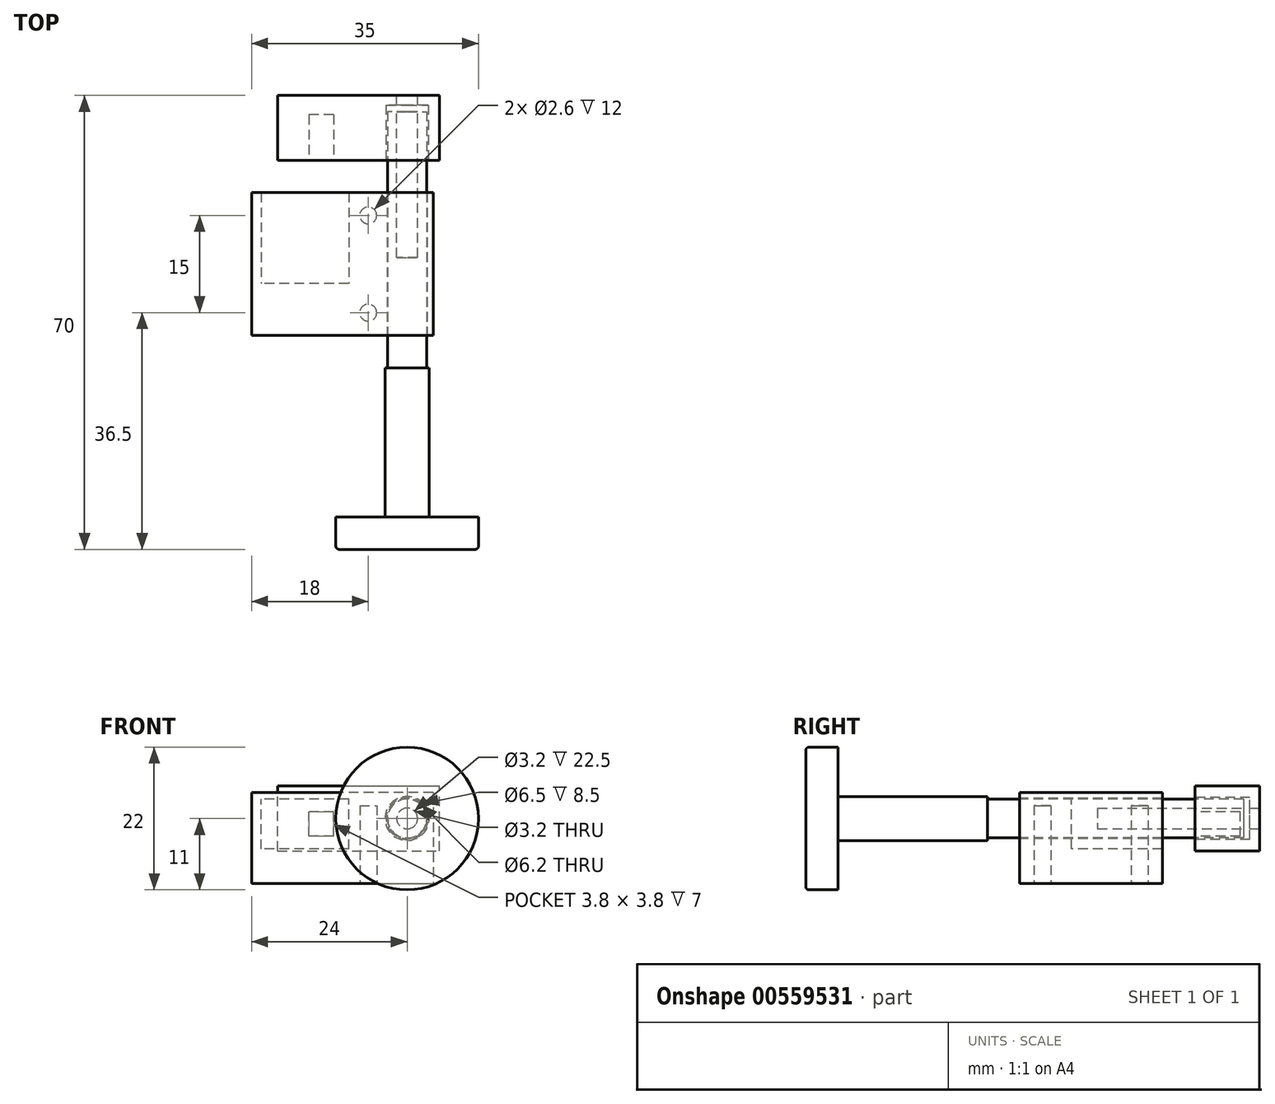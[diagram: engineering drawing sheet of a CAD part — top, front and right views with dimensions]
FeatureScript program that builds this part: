
annotation { "Feature Type Name" : "Feature", "Feature Type Description" : "" }
export const myFeature = defineFeature(function(context is Context, id is Id, definition is map)
    precondition{}
    {
        {
            var Q0;
            Q0=qCreatedBy(makeId("Front.planeOp"),FACE);
            var sketch = newSketch(context, id + "F0", { "sketchPlane" : qUnion([Q0])});
            skLineSegment(sketch, "E0.bottom", {"start": v(-22, -4.85) * mm, "end": v(-50, -4.85) * mm});
            skLineSegment(sketch, "E0.top", {"start": v(-22, 4.85) * mm, "end": v(-50, 4.85) * mm});
            skLineSegment(sketch, "E0.left", {"start": v(-22, -4.85) * mm, "end": v(-22, 4.85) * mm});
            skLineSegment(sketch, "E0.right", {"start": v(-50, -4.85) * mm, "end": v(-50, 4.85) * mm});
            skPoint(sketch, "E0.middle", {"position": v(-36, 0) * mm});
            skLineSegment(sketch, "E1.bottom", {"start": v(-35, -3.85) * mm, "end": v(-48.5, -3.85) * mm});
            skLineSegment(sketch, "E1.top", {"start": v(-35, 3.85) * mm, "end": v(-48.5, 3.85) * mm});
            skLineSegment(sketch, "E1.left", {"start": v(-35, -3.85) * mm, "end": v(-35, 3.85) * mm});
            skLineSegment(sketch, "E1.right", {"start": v(-48.5, -3.85) * mm, "end": v(-48.5, 3.85) * mm});
            skPoint(sketch, "E1.middle", {"position": v(-41.75, 0) * mm});
            skLineSegment(sketch, "E2.bottom", {"start": v(-50, -4.85) * mm, "end": v(-22, -4.85) * mm});
            skLineSegment(sketch, "E2.top", {"start": v(-50, -9.15) * mm, "end": v(-22, -9.15) * mm});
            skLineSegment(sketch, "E2.left", {"start": v(-50, -4.85) * mm, "end": v(-50, -9.15) * mm});
            skLineSegment(sketch, "E2.right", {"start": v(-22, -4.85) * mm, "end": v(-22, -9.15) * mm});
            skCircle(sketch, "E3", {"center": v(-26, 0.85) * mm, "radius": 3.1 * mm});
            skSolve(sketch);
        }
        {
            var Q0;
            Q0=qSketchRegion(id+"F0",true);
            extrude(context, id + "F1", {"entities" : qUnion([Q0]), "oppositeDirection" : true, "depth" : 22 * mm});
        }
        {
            var Q0;
            Q0=makeQuery(id+"F1.opExtrude","CAP_FACE",FACE,{"disambiguationData":[OSD([sQuery(id+"F0.wireOp",EDGE,"E0.bottom"),sQuery(id+"F0.wireOp",EDGE,"E0.top"),sQuery(id+"F0.wireOp",EDGE,"E0.left"),sQuery(id+"F0.wireOp",EDGE,"E0.right"),sQuery(id+"F0.wireOp",EDGE,"E1.bottom"),sQuery(id+"F0.wireOp",EDGE,"E1.top"),sQuery(id+"F0.wireOp",EDGE,"E1.left"),sQuery(id+"F0.wireOp",EDGE,"E1.right"),sQuery(id+"F0.wireOp",EDGE,"IlVQ0T6Q-kpas-WKJO-rE1o-QIE4vgIgB8Sl")])],"isStart":true});
            var sketch = newSketch(context, id + "F2", { "sketchPlane" : qUnion([Q0])});
            skLineSegment(sketch, "E4.bottom", {"start": v(-48.5, 3.85) * mm, "end": v(-35, 3.85) * mm});
            skLineSegment(sketch, "E4.top", {"start": v(-48.5, -3.85) * mm, "end": v(-35, -3.85) * mm});
            skLineSegment(sketch, "E4.left", {"start": v(-35, 3.85) * mm, "end": v(-35, -3.85) * mm});
            skLineSegment(sketch, "E4.right", {"start": v(-48.5, 3.85) * mm, "end": v(-48.5, -3.85) * mm});
            skSolve(sketch);
        }
        {
            var Q0;
            Q0=qSketchRegion(id+"F2",true);
            extrude(context, id + "F3", {"entities" : qUnion([Q0]), "operationType" : NewBodyOperationType.ADD, "oppositeDirection" : true, "depth" : 8 * mm});
        }
        {
            var Q0;
            Q0=makeQuery(id+"F1.opExtrude","SWEPT_FACE",FACE,{"disambiguationData":[OSD([sQuery(id+"F0.wireOp",EDGE,"E2.top")])]});
            var sketch = newSketch(context, id + "F4", { "sketchPlane" : qUnion([Q0])});
            skCircle(sketch, "E5", {"center": v(-32, -3.5) * mm, "radius": 1.3 * mm});
            skCircle(sketch, "E6", {"center": v(-32, -18.5) * mm, "radius": 1.3 * mm});
            skSolve(sketch);
        }
        {
            var Q0;
            Q0=qSketchRegion(id+"F4",true);
            extrude(context, id + "F5", {"entities" : qUnion([Q0]), "operationType" : NewBodyOperationType.REMOVE, "oppositeDirection" : true, "depth" : 12 * mm});
        }
        {
            var Q0;
            Q0=makeQuery(id+"F1.opExtrude","CAP_FACE",FACE,{"disambiguationData":[OSD([sQuery(id+"F0.wireOp",EDGE,"E0.top"),sQuery(id+"F0.wireOp",EDGE,"E0.left"),sQuery(id+"F0.wireOp",EDGE,"E0.right"),sQuery(id+"F0.wireOp",EDGE,"E1.bottom"),sQuery(id+"F0.wireOp",EDGE,"E1.top"),sQuery(id+"F0.wireOp",EDGE,"E1.left"),sQuery(id+"F0.wireOp",EDGE,"E1.right"),sQuery(id+"F0.wireOp",EDGE,"E2.top"),sQuery(id+"F0.wireOp",EDGE,"E2.left"),sQuery(id+"F0.wireOp",EDGE,"E2.right"),sQuery(id+"F0.wireOp",EDGE,"E3")])],"isStart":false});
            cPlane(context, id + "F6", {"entities" : qUnion([Q0]), "cplaneType" : CPlaneType.OFFSET, "offset" : 5 * mm, "width" : 150 * mm, "height" : 150 * mm});
        }
        {
            var Q0;
            Q0=qCreatedBy(makeId("Front.planeOp"),FACE);
            cPlane(context, id + "F7", {"entities" : qUnion([Q0]), "cplaneType" : CPlaneType.OFFSET, "offset" : 28 * mm, "width" : 150 * mm, "height" : 150 * mm});
        }
        {
            var Q0;
            Q0=qCreatedBy(id+"F7.planeOp",FACE);
            var sketch = newSketch(context, id + "F8", { "sketchPlane" : qUnion([Q0])});
            skCircle(sketch, "E7", {"center": v(-26, 0.85) * mm, "radius": 11 * mm});
            skSolve(sketch);
        }
        {
            var Q0;
            Q0=qSketchRegion(id+"F8",true);
            extrude(context, id + "F9", {"entities" : qUnion([Q0]), "depth" : 5 * mm});
        }
        {
            var Q0;
            Q0=makeQuery(id+"F9.opExtrude","CAP_FACE",FACE,{"disambiguationData":[OSD([sQuery(id+"F8.wireOp",EDGE,"E7")])],"isStart":true});
            var sketch = newSketch(context, id + "F10", { "sketchPlane" : qUnion([Q0])});
            skCircle(sketch, "E8", {"center": v(26, 0.85) * mm, "radius": 3 * mm});
            skSolve(sketch);
        }
        {
            var Q0;
            Q0=qSketchRegion(id+"F10",true);
            extrude(context, id + "F11", {"entities" : qUnion([Q0]), "operationType" : NewBodyOperationType.ADD, "depth" : 55 * mm});
        }
        {
            var Q0;
            Q0=qCreatedBy(id+"F6.planeOp",FACE);
            var sketch = newSketch(context, id + "F12", { "sketchPlane" : qUnion([Q0])});
            skLineSegment(sketch, "E9.bottom", {"start": v(46, -4.15) * mm, "end": v(21, -4.15) * mm});
            skLineSegment(sketch, "E9.top", {"start": v(46, 5.85) * mm, "end": v(21, 5.85) * mm});
            skLineSegment(sketch, "E9.left", {"start": v(46, -4.15) * mm, "end": v(46, 5.85) * mm});
            skLineSegment(sketch, "E9.right", {"start": v(21, -4.15) * mm, "end": v(21, 5.85) * mm});
            skSolve(sketch);
        }
        {
            var Q0;
            Q0=qSketchRegion(id+"F12",true);
            extrude(context, id + "F13", {"entities" : qUnion([Q0]), "depth" : 10 * mm});
        }
        {
            var Q0;
            Q0=makeQuery(id+"F13.opExtrude","CAP_FACE",FACE,{"disambiguationData":[OSD([sQuery(id+"F12.wireOp",EDGE,"E9.bottom"),sQuery(id+"F12.wireOp",EDGE,"E9.top"),sQuery(id+"F12.wireOp",EDGE,"E9.left"),sQuery(id+"F12.wireOp",EDGE,"E9.right")])],"isStart":true});
            var sketch = newSketch(context, id + "F14", { "sketchPlane" : qUnion([Q0])});
            skLineSegment(sketch, "E10.bottom", {"start": v(-37.35, -1.9) * mm, "end": v(-41.15, -1.9) * mm});
            skLineSegment(sketch, "E10.top", {"start": v(-37.35, 1.9) * mm, "end": v(-41.15, 1.9) * mm});
            skLineSegment(sketch, "E10.left", {"start": v(-37.35, -1.9) * mm, "end": v(-37.35, 1.9) * mm});
            skLineSegment(sketch, "E10.right", {"start": v(-41.15, -1.9) * mm, "end": v(-41.15, 1.9) * mm});
            skPoint(sketch, "E10.middle", {"position": v(-39.25, 0) * mm});
            skCircle(sketch, "E11", {"center": v(-26, 0.85) * mm, "radius": 3.25 * mm});
            skSolve(sketch);
        }
        {
            var Q0;
            Q0=makeQuery(id+"F14.imprint","IMPRINT",FACE,{"disambiguationData":[TD([[makeQuery(id+"F14.imprint","IMPRINT",EDGE,{"derivedFrom":sQuery(id+"F14.wireOp",EDGE,"E10.bottom")}),-1.0]])]});
            extrude(context, id + "F15", {"entities" : qUnion([Q0]), "operationType" : NewBodyOperationType.REMOVE, "oppositeDirection" : true, "depth" : 7 * mm});
        }
        {
            var Q0;
            Q0=makeQuery(id+"F14.imprint","IMPRINT",FACE,{"disambiguationData":[TD([[makeQuery(id+"F14.imprint","IMPRINT",EDGE,{"derivedFrom":sQuery(id+"F14.wireOp",EDGE,"E11")}),1.0]])]});
            extrude(context, id + "F16", {"entities" : qUnion([Q0]), "operationType" : NewBodyOperationType.REMOVE, "oppositeDirection" : true, "depth" : 8.5 * mm});
        }
        {
            var Q0;
            Q0=makeQuery(id+"F8.imprint","IMPRINT",FACE,{"disambiguationData":[TD([[makeQuery(id+"F8.imprint","IMPRINT",EDGE,{"derivedFrom":sQuery(id+"F8.wireOp",EDGE,"E7")}),1.0]])]});
            var sketch = newSketch(context, id + "F17", { "sketchPlane" : qUnion([Q0])});
            skCircle(sketch, "E12", {"center": v(-26, 0.85) * mm, "radius": 3.4 * mm});
            skSolve(sketch);
        }
        {
            var Q0;
            Q0=qSketchRegion(id+"F17",true);
            extrude(context, id + "F18", {"entities" : qUnion([Q0]), "operationType" : NewBodyOperationType.ADD, "oppositeDirection" : true, "depth" : 23 * mm});
        }
        {
            var Q0;
            Q0=makeQuery(id+"F11.opExtrude","CAP_FACE",FACE,{"disambiguationData":[OSD([sQuery(id+"F10.wireOp",EDGE,"E8")])],"isStart":false});
            var sketch = newSketch(context, id + "F19", { "sketchPlane" : qUnion([Q0])});
            skCircle(sketch, "E13", {"center": v(26, 0.85) * mm, "radius": 3 * mm});
            skSolve(sketch);
        }
        {
            var Q0;
            Q0=qSketchRegion(id+"F19",true);
            extrude(context, id + "F20", {"entities" : qUnion([Q0]), "operationType" : NewBodyOperationType.ADD, "depth" : 7.5 * mm});
        }
        {
            var Q0;
            Q0=makeQuery(id+"F20.opExtrude","CAP_FACE",FACE,{"disambiguationData":[OSD([sQuery(id+"F19.wireOp",EDGE,"E13")])],"isStart":false});
            var sketch = newSketch(context, id + "F21", { "sketchPlane" : qUnion([Q0])});
            skCircle(sketch, "E14", {"center": v(26, 0.85) * mm, "radius": 1.3 * mm});
            skSolve(sketch);
        }
        {
            var Q0;
            Q0=qSketchRegion(id+"F21",true);
            extrude(context, id + "F22", {"entities" : qUnion([Q0]), "operationType" : NewBodyOperationType.REMOVE, "oppositeDirection" : true, "depth" : 12 * mm});
        }
        {
            var Q0;
            Q0=makeQuery(id+"F13.opExtrude","CAP_FACE",FACE,{"disambiguationData":[OSD([sQuery(id+"F12.wireOp",EDGE,"E9.bottom"),sQuery(id+"F12.wireOp",EDGE,"E9.top"),sQuery(id+"F12.wireOp",EDGE,"E9.left"),sQuery(id+"F12.wireOp",EDGE,"E9.right")])],"isStart":false});
            var sketch = newSketch(context, id + "F23", { "sketchPlane" : qUnion([Q0])});
            skCircle(sketch, "E15", {"center": v(26, 0.85) * mm, "radius": 1.6 * mm});
            skSolve(sketch);
        }
        {
            var Q0;
            Q0=qSketchRegion(id+"F23",true);
            extrude(context, id + "F24", {"entities" : qUnion([Q0]), "operationType" : NewBodyOperationType.REMOVE, "oppositeDirection" : true, "depth" : 25 * mm});
        }
        {
            var Q0;
            Q0=makeQuery(id+"F9.opExtrude","CAP_EDGE",EDGE,{"disambiguationData":[OSD([sQuery(id+"F8.wireOp",EDGE,"E7")])],"isStart":false});
            fillet(context, id + "F25", {"entities" : qUnion([Q0]), "radius" : 0.5 * mm, "tangentPropagation" : true, "allowEdgeOverflow" : false});
        }
    });
